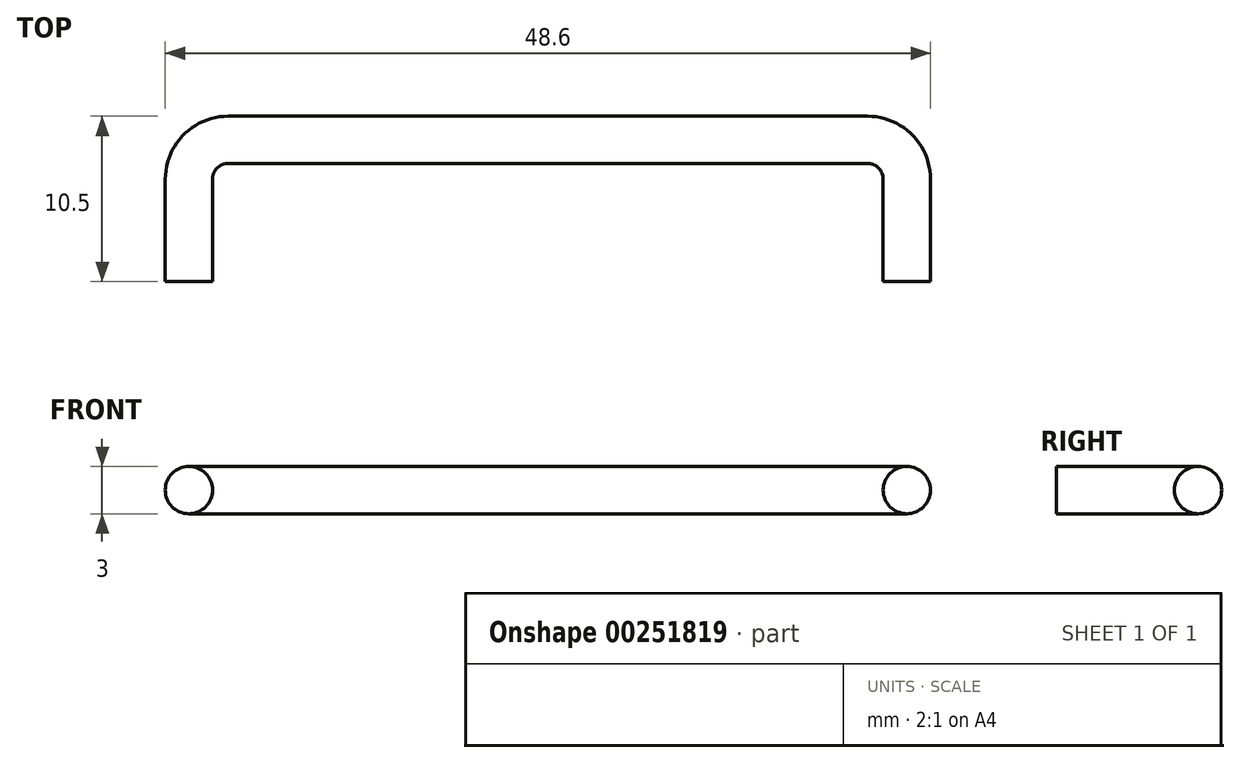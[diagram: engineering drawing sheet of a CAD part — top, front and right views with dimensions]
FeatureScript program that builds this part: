
annotation { "Feature Type Name" : "Feature", "Feature Type Description" : "" }
export const myFeature = defineFeature(function(context is Context, id is Id, definition is map)
    precondition{}
    {
        {
            var Q0;
            Q0=qCreatedBy(makeId("Top.planeOp"),FACE);
            var sketch = newSketch(context, id + "F0", { "sketchPlane" : qUnion([Q0])});
            skLineSegment(sketch, "E0", {"start": v(0, 5.12) * mm, "end": v(0, -5.08) * mm, "construction": true});
            skLineSegment(sketch, "E1.0", {"start": v(22.8, -9) * mm, "end": v(22.8, -2.5) * mm});
            skLineSegment(sketch, "E1.1", {"start": v(-22.8, -9) * mm, "end": v(-22.8, -2.5) * mm});
            skArc(sketch, "E1.2", {"start": v(-22.8, -2.5) * mm, "mid": v(-22.07, -0.73) * mm, "end": v(-20.3, 0) * mm});
            skLineSegment(sketch, "E1.3", {"start": v(-20.3, 0) * mm, "end": v(20.3, 0) * mm});
            skArc(sketch, "E1.4", {"start": v(22.8, -2.5) * mm, "mid": v(22.07, -0.73) * mm, "end": v(20.3, 0) * mm});
            skPoint(sketch, "E2.MirrorCS.end.orphan", {"position": v(-20.3, 1.5) * mm});
            skPoint(sketch, "E2.MirrorCS.start.orphan", {"position": v(-24.3, -2.5) * mm});
            skPoint(sketch, "E3.MirrorCS.start.orphan", {"position": v(-24.3, -9) * mm});
            skPoint(sketch, "E4.MirrorCS.end.orphan", {"position": v(-21.3, -9) * mm});
            skPoint(sketch, "E4.MirrorCS.start.orphan", {"position": v(-21.3, -2.5) * mm});
            skPoint(sketch, "E5.MirrorCS.end.orphan", {"position": v(-20.3, -1.5) * mm});
            skPoint(sketch, "E6.end.orphan", {"position": v(20.3, -1.5) * mm});
            skPoint(sketch, "E7.start.orphan", {"position": v(21.3, -2.5) * mm});
            skPoint(sketch, "E8.start.orphan", {"position": v(24.3, -2.5) * mm});
            skPoint(sketch, "E9.right.start.orphan", {"position": v(20.3, 1.5) * mm});
            skPoint(sketch, "E10.orphan", {"position": v(24.3, -9) * mm});
            skPoint(sketch, "E11.start.orphan", {"position": v(21.3, -9) * mm});
            skSolve(sketch);
        }
        {
            var Q0;
            Q0=sQuery(id+"F0.wireOp",EDGE,"E1.0");
            var Q1;
            Q1=sQuery(id+"F0.wireOp",VERTEX,"E1.0.start");
            cPlane(context, id + "F1", {"entities" : qUnion([Q0, Q1]), "cplaneType" : CPlaneType.CURVE_POINT, "offset" : 25 * mm, "width" : 150 * mm, "height" : 150 * mm});
        }
        {
            var Q0;
            Q0=qCreatedBy(id+"F1.planeOp",FACE);
            var sketch = newSketch(context, id + "F2", { "sketchPlane" : qUnion([Q0])});
            skCircle(sketch, "E12", {"center": v(-22.8, 0) * mm, "radius": 1.5 * mm});
            skSolve(sketch);
        }
        {
            var Q0;
            Q0=makeQuery(id+"F2.imprint","IMPRINT",FACE,{"disambiguationData":[TD([[makeQuery(id+"F2.imprint","IMPRINT",EDGE,{"derivedFrom":sQuery(id+"F2.wireOp",EDGE,"E12")}),1.0]])]});
            var Q1;
            Q1=sQuery(id+"F0.wireOp",EDGE,"E1.0");
            var Q2;
            Q2=sQuery(id+"F0.wireOp",EDGE,"E1.4");
            var Q3;
            Q3=sQuery(id+"F0.wireOp",EDGE,"E1.3");
            var Q4;
            Q4=sQuery(id+"F0.wireOp",EDGE,"E1.2");
            var Q5;
            Q5=sQuery(id+"F0.wireOp",EDGE,"E1.1");
            sweep(context, id + "F3", {"profiles" : qUnion([Q0]), "path" : qUnion([Q1, Q2, Q3, Q4, Q5])});
        }
    });
